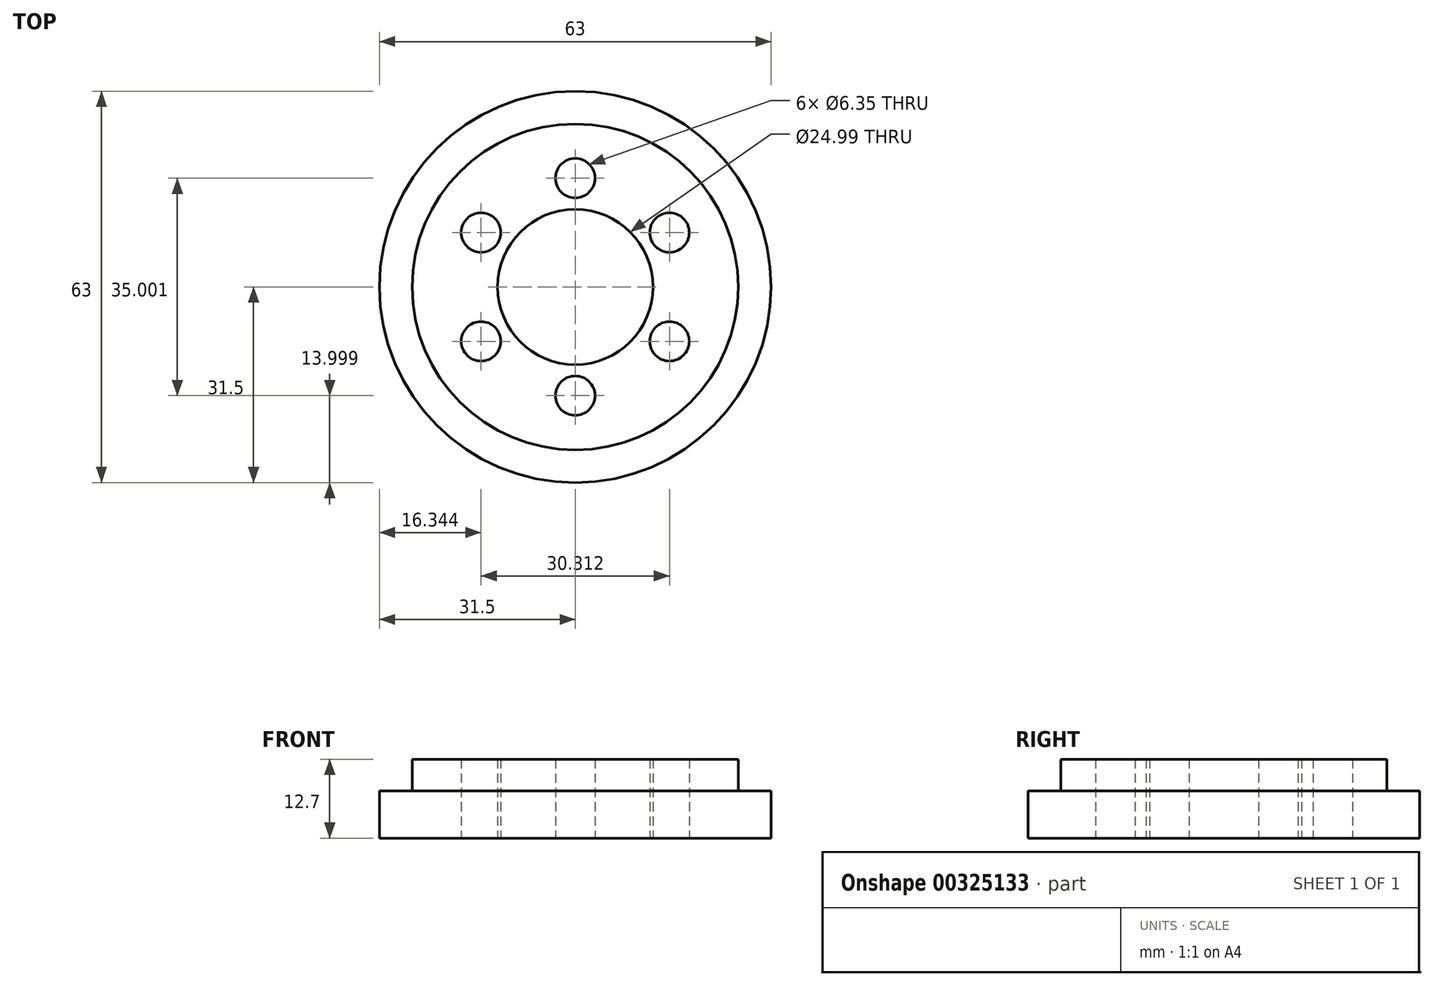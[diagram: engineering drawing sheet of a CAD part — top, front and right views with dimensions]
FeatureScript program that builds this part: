
annotation { "Feature Type Name" : "Feature", "Feature Type Description" : "" }
export const myFeature = defineFeature(function(context is Context, id is Id, definition is map)
    precondition{}
    {
        {
            var Q0;
            Q0=qCreatedBy(makeId("Top.planeOp"),FACE);
            var sketch = newSketch(context, id + "F0", { "sketchPlane" : qUnion([Q0])});
            skCircle(sketch, "E0", {"center": v(0, 0) * mm, "radius": 12.5 * mm});
            skCircle(sketch, "E1", {"center": v(0, 0) * mm, "radius": 31.5 * mm});
            skLineSegment(sketch, "E2", {"start": v(0, 0) * mm, "end": v(0, 17.5) * mm});
            skLineSegment(sketch, "E3", {"start": v(0, 0) * mm, "end": v(15.16, 8.75) * mm});
            skPoint(sketch, "E3.endSnap0", {"position": v(0, 8.75) * mm});
            skLineSegment(sketch, "E4", {"start": v(0, 0) * mm, "end": v(-15.16, 8.75) * mm});
            skLineSegment(sketch, "E5", {"start": v(0, 0) * mm, "end": v(0, -17.5) * mm});
            skLineSegment(sketch, "E6", {"start": v(0, 0) * mm, "end": v(15.16, -8.75) * mm});
            skLineSegment(sketch, "E7", {"start": v(0, 0) * mm, "end": v(-15.16, -8.75) * mm});
            skCircle(sketch, "E8", {"center": v(0, 17.5) * mm, "radius": 3.18 * mm});
            skCircle(sketch, "E9", {"center": v(15.16, 8.75) * mm, "radius": 3.18 * mm});
            skCircle(sketch, "E10", {"center": v(15.16, -8.75) * mm, "radius": 3.18 * mm});
            skCircle(sketch, "E11", {"center": v(0, -17.5) * mm, "radius": 3.18 * mm});
            skCircle(sketch, "E12", {"center": v(-15.16, -8.75) * mm, "radius": 3.18 * mm});
            skCircle(sketch, "E13", {"center": v(-15.16, 8.75) * mm, "radius": 3.18 * mm});
            skSolve(sketch);
        }
        {
            var Q0;
            Q0=makeQuery(id+"F0.imprint","IMPRINT",FACE,{"disambiguationData":[TD([[makeQuery(id+"F0.imprint","IMPRINT",EDGE,{"derivedFrom":sQuery(id+"F0.wireOp",EDGE,"E0")}),-1.0]])]});
            extrude(context, id + "F1", {"entities" : qUnion([Q0]), "depth" : 7.62 * mm});
        }
        {
            var Q0;
            Q0=makeQuery(id+"F1.opExtrude","CAP_FACE",FACE,{"disambiguationData":[OSD([sQuery(id+"F0.wireOp",EDGE,"E0"),sQuery(id+"F0.wireOp",EDGE,"E1")])],"isStart":false});
            var sketch = newSketch(context, id + "F2", { "sketchPlane" : qUnion([Q0])});
            skCircle(sketch, "E14", {"center": v(0, 0) * mm, "radius": 26.23 * mm});
            skSolve(sketch);
        }
        {
            var Q0;
            Q0=makeQuery(id+"F2.imprint","IMPRINT",FACE,{"disambiguationData":[TD([[makeQuery(id+"F2.imprint","IMPRINT",EDGE,{"derivedFrom":sQuery(id+"F2.wireOp",EDGE,"E14")}),1.0]])]});
            extrude(context, id + "F3", {"entities" : qUnion([Q0]), "operationType" : NewBodyOperationType.ADD, "depth" : 5.08 * mm});
        }
    });
